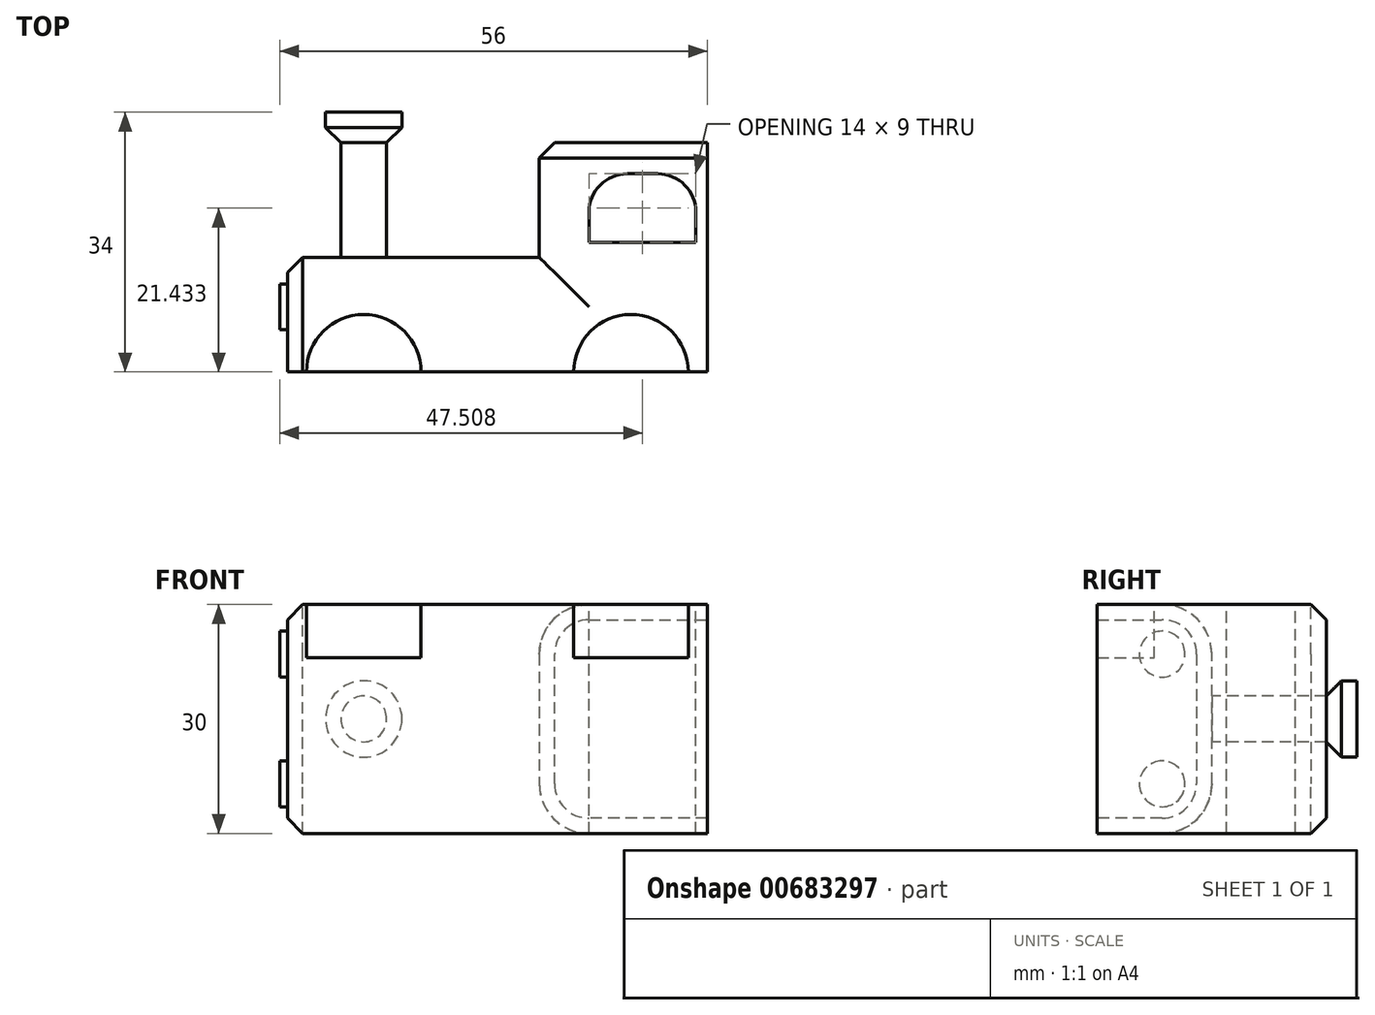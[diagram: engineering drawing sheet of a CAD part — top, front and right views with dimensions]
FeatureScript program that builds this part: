
annotation { "Feature Type Name" : "Feature", "Feature Type Description" : "" }
export const myFeature = defineFeature(function(context is Context, id is Id, definition is map)
    precondition{}
    {
        {
            var Q0;
            Q0=qCreatedBy(makeId("Top.planeOp"),FACE);
            var sketch = newSketch(context, id + "F0", { "sketchPlane" : qUnion([Q0])});
            skLineSegment(sketch, "E0.bottom", {"start": v(-27.5, 15) * mm, "end": v(27.5, 15) * mm});
            skLineSegment(sketch, "E0.top", {"start": v(-27.5, -15) * mm, "end": v(27.5, -15) * mm});
            skLineSegment(sketch, "E0.left", {"start": v(-27.5, 15) * mm, "end": v(-27.5, -15) * mm});
            skLineSegment(sketch, "E0.right", {"start": v(27.5, 15) * mm, "end": v(27.5, -15) * mm});
            skPoint(sketch, "E0.middle", {"position": v(0, 0) * mm});
            skLineSegment(sketch, "E1", {"start": v(-27.5, 0) * mm, "end": v(5.5, 0) * mm});
            skLineSegment(sketch, "E2", {"start": v(5.5, 0) * mm, "end": v(5.5, 15) * mm});
            skSolve(sketch);
        }
        {
            var Q0;
            {var subQ2=sQuery(id+"F0.wireOp",EDGE,"E0.top");Q0=makeQuery(id+"F0.imprint","IMPRINT",FACE,{"disambiguationData":[TD([[makeQuery(id+"F0.imprint","IMPRINT",EDGE,{"derivedFrom":subQ2}),1.0]])]});}
            extrude(context, id + "F1", {"entities" : qUnion([Q0]), "endBound" : BoundingType.SYMMETRIC, "depth" : 30 * mm, "offsetDistance" : 25 * mm});
        }
        {
            var Q0;
            Q0=makeQuery(id+"F1.opExtrude","CAP_FACE",FACE,{"disambiguationData":[OSD([sQuery(id+"F0.wireOp",EDGE,"E0.bottom"),sQuery(id+"F0.wireOp",EDGE,"E0.top"),sQuery(id+"F0.wireOp",EDGE,"E0.left"),sQuery(id+"F0.wireOp",EDGE,"E0.right"),sQuery(id+"F0.wireOp",EDGE,"E1"),sQuery(id+"F0.wireOp",EDGE,"E2")])],"isStart":false});
            var sketch = newSketch(context, id + "F2", { "sketchPlane" : qUnion([Q0])});
            skCircle(sketch, "E3", {"center": v(-17.5, -15) * mm, "radius": 7.5 * mm});
            skCircle(sketch, "E4.1.0.0", {"center": v(17.5, -15) * mm, "radius": 7.5 * mm});
            skLineSegment(sketch, "E4.direction1", {"start": v(-17.5, -15) * mm, "end": v(17.5, -15) * mm, "construction": true});
            skSolve(sketch);
        }
        {
            var Q0;
            {var subQ0=sQuery(id+"F2.wireOp",EDGE,"E3");var subQ1=makeQuery(id+"F1.opExtrude","CAP_EDGE",EDGE,{"disambiguationData":[OSD([sQuery(id+"F0.wireOp",EDGE,"E0.top")])],"isStart":false});var subQ2=makeQuery(id+"F2.imprint","INTERSECT",VERTEX,{"disambiguationData":[OD(0.0)],"derivedFrom":[subQ1,subQ0]});Q0=makeQuery(id+"F2.imprint","IMPRINT",FACE,{"disambiguationData":[TD([[makeQuery(id+"F2.imprint","IMPRINT",EDGE,{"disambiguationData":[TD([[subQ2,1.0]])],"derivedFrom":subQ0}),1.0]])]});}
            var Q1;
            {var subQ0=sQuery(id+"F2.wireOp",EDGE,"E4.1.0.0");var subQ1=makeQuery(id+"F1.opExtrude","CAP_EDGE",EDGE,{"disambiguationData":[OSD([sQuery(id+"F0.wireOp",EDGE,"E0.top")])],"isStart":false});var subQ2=makeQuery(id+"F2.imprint","INTERSECT",VERTEX,{"disambiguationData":[OD(0.0)],"derivedFrom":[subQ1,subQ0]});Q1=makeQuery(id+"F2.imprint","IMPRINT",FACE,{"disambiguationData":[TD([[makeQuery(id+"F2.imprint","IMPRINT",EDGE,{"disambiguationData":[TD([[subQ2,-1.0]])],"derivedFrom":subQ0}),1.0]])]});}
            extrude(context, id + "F3", {"entities" : qUnion([Q0, Q1]), "operationType" : NewBodyOperationType.REMOVE, "oppositeDirection" : true, "depth" : 7 * mm, "offsetDistance" : 25 * mm});
        }
        {
            var Q0;
            Q0=makeQuery(id+"F1.opExtrude","CAP_EDGE",EDGE,{"disambiguationData":[OSD([sQuery(id+"F0.wireOp",EDGE,"E1")])],"isStart":false});
            var Q1;
            Q1=makeQuery(id+"F1.opExtrude","CAP_EDGE",EDGE,{"disambiguationData":[OSD([sQuery(id+"F0.wireOp",EDGE,"E1")])],"isStart":true});
            var Q2;
            Q2=makeQuery(id+"F1.opExtrude","CAP_EDGE",EDGE,{"disambiguationData":[OSD([sQuery(id+"F0.wireOp",EDGE,"E2")])],"isStart":false});
            var Q3;
            Q3=makeQuery(id+"F1.opExtrude","CAP_EDGE",EDGE,{"disambiguationData":[OSD([sQuery(id+"F0.wireOp",EDGE,"E2")])],"isStart":true});
            fillet(context, id + "F4", {"entities" : qUnion([Q0, Q1, Q2, Q3]), "radius" : 6.5 * mm, "tangentPropagation" : true, "allowEdgeOverflow" : false});
        }
        {
            var Q0;
            Q0=makeQuery(id+"F1.opExtrude","SWEPT_EDGE",EDGE,{"disambiguationData":[OSD([sQuery(id+"F0.wireOp",EDGE,"E0.bottom"),sQuery(id+"F0.wireOp",EDGE,"E2")])]});
            var Q1;
            Q1=makeQuery(id+"F1.opExtrude","SWEPT_EDGE",EDGE,{"disambiguationData":[OSD([sQuery(id+"F0.wireOp",EDGE,"E0.left"),sQuery(id+"F0.wireOp",EDGE,"E1")])]});
            chamfer(context, id + "F5", {"entities" : qUnion([Q0, Q1]), "width" : 2 * mm, "tangentPropagation" : true});
        }
        {
            var Q0;
            Q0=makeQuery(id+"F1.opExtrude","CAP_FACE",FACE,{"disambiguationData":[OSD([sQuery(id+"F0.wireOp",EDGE,"E0.bottom"),sQuery(id+"F0.wireOp",EDGE,"E0.top"),sQuery(id+"F0.wireOp",EDGE,"E0.left"),sQuery(id+"F0.wireOp",EDGE,"E0.right"),sQuery(id+"F0.wireOp",EDGE,"E1"),sQuery(id+"F0.wireOp",EDGE,"E2")])],"isStart":false});
            var sketch = newSketch(context, id + "F6", { "sketchPlane" : qUnion([Q0])});
            skLineSegment(sketch, "E5.bottom", {"start": v(26, 1.93) * mm, "end": v(12, 1.93) * mm});
            skLineSegment(sketch, "E5.top", {"start": v(26, 10.93) * mm, "end": v(12, 10.93) * mm});
            skLineSegment(sketch, "E5.left", {"start": v(26, 1.93) * mm, "end": v(26, 10.93) * mm});
            skLineSegment(sketch, "E5.right", {"start": v(12, 1.93) * mm, "end": v(12, 10.93) * mm});
            skPoint(sketch, "E5.middle", {"position": v(19, 6.43) * mm});
            skSolve(sketch);
        }
        {
            var Q0;
            Q0=makeQuery(id+"F6.imprint","IMPRINT",FACE,{"disambiguationData":[TD([[makeQuery(id+"F6.imprint","IMPRINT",EDGE,{"derivedFrom":sQuery(id+"F6.wireOp",EDGE,"E5.bottom")}),-1.0]])]});
            extrude(context, id + "F7", {"entities" : qUnion([Q0]), "operationType" : NewBodyOperationType.REMOVE, "endBound" : BoundingType.THROUGH_ALL, "oppositeDirection" : true, "depth" : 25 * mm, "offsetDistance" : 25 * mm});
        }
        {
            var Q0;
            Q0=makeQuery(id+"F7.boolean.opBoolean","COPY",EDGE,{"derivedFrom":makeQuery(id+"F7.opExtrude","CAP_EDGE",EDGE,{"disambiguationData":[OSD([sQuery(id+"F6.wireOp",EDGE,"E5.bottom")])],"isStart":true})});
            var Q1;
            Q1=makeQuery(id+"F7.boolean.opBoolean","COPY",EDGE,{"derivedFrom":makeQuery(id+"F7.opExtrude","SWEPT_EDGE",EDGE,{"disambiguationData":[OSD([sQuery(id+"F6.wireOp",EDGE,"E5.top"),sQuery(id+"F6.wireOp",EDGE,"E5.left")])]})});
            var Q2;
            Q2=makeQuery(id+"F7.boolean.opBoolean","COPY",EDGE,{"derivedFrom":makeQuery(id+"F7.opExtrude","SWEPT_EDGE",EDGE,{"disambiguationData":[OSD([sQuery(id+"F6.wireOp",EDGE,"E5.top"),sQuery(id+"F6.wireOp",EDGE,"E5.right")])]})});
            fillet(context, id + "F8", {"entities" : qUnion([Q0, Q1, Q2]), "radius" : 5 * mm, "tangentPropagation" : true, "allowEdgeOverflow" : false});
        }
        {
            var Q0;
            Q0=makeQuery(id+"F1.opExtrude","SWEPT_FACE",FACE,{"disambiguationData":[OSD([sQuery(id+"F0.wireOp",EDGE,"E0.left")])]});
            var sketch = newSketch(context, id + "F9", { "sketchPlane" : qUnion([Q0])});
            skCircle(sketch, "E6", {"center": v(6.5, 8.5) * mm, "radius": 3 * mm});
            skCircle(sketch, "E7", {"center": v(6.5, -8.5) * mm, "radius": 3 * mm});
            skSolve(sketch);
        }
        {
            var Q0;
            Q0 = qSketchRegion(id + "F9", true);
            extrude(context, id + "F10", {"entities" : qUnion([Q0]), "operationType" : NewBodyOperationType.ADD, "depth" : 1 * mm, "offsetDistance" : 25 * mm});
        }
        {
            var Q0;
            Q0=makeQuery(id+"F1.opExtrude","SWEPT_FACE",FACE,{"disambiguationData":[OSD([sQuery(id+"F0.wireOp",EDGE,"E1")])]});
            var sketch = newSketch(context, id + "F11", { "sketchPlane" : qUnion([Q0])});
            skCircle(sketch, "E8", {"center": v(17.5, 0) * mm, "radius": 3 * mm});
            skSolve(sketch);
        }
        {
            var Q0;
            Q0 = qSketchRegion(id + "F11", true);
            extrude(context, id + "F12", {"entities" : qUnion([Q0]), "operationType" : NewBodyOperationType.ADD, "depth" : 15 * mm, "offsetDistance" : 25 * mm});
        }
        {
            var Q0;
            Q0=makeQuery(id+"F12.opExtrude","CAP_FACE",FACE,{"disambiguationData":[OSD([sQuery(id+"F11.wireOp",EDGE,"E8")])],"isStart":false});
            var sketch = newSketch(context, id + "F13", { "sketchPlane" : qUnion([Q0])});
            skCircle(sketch, "E9", {"center": v(17.5, 0) * mm, "radius": 5 * mm});
            skSolve(sketch);
        }
        {
            var Q0;
            Q0 = qSketchRegion(id + "F13", true);
            extrude(context, id + "F14", {"entities" : qUnion([Q0]), "operationType" : NewBodyOperationType.ADD, "depth" : 4 * mm, "offsetDistance" : 25 * mm});
        }
        {
            var Q0;
            Q0=makeQuery(id+"F14.opExtrude","CAP_EDGE",EDGE,{"disambiguationData":[OSD([sQuery(id+"F13.wireOp",EDGE,"E9")])],"isStart":true});
            chamfer(context, id + "F15", {"entities" : qUnion([Q0]), "width" : 2 * mm, "tangentPropagation" : true});
        }
    });
